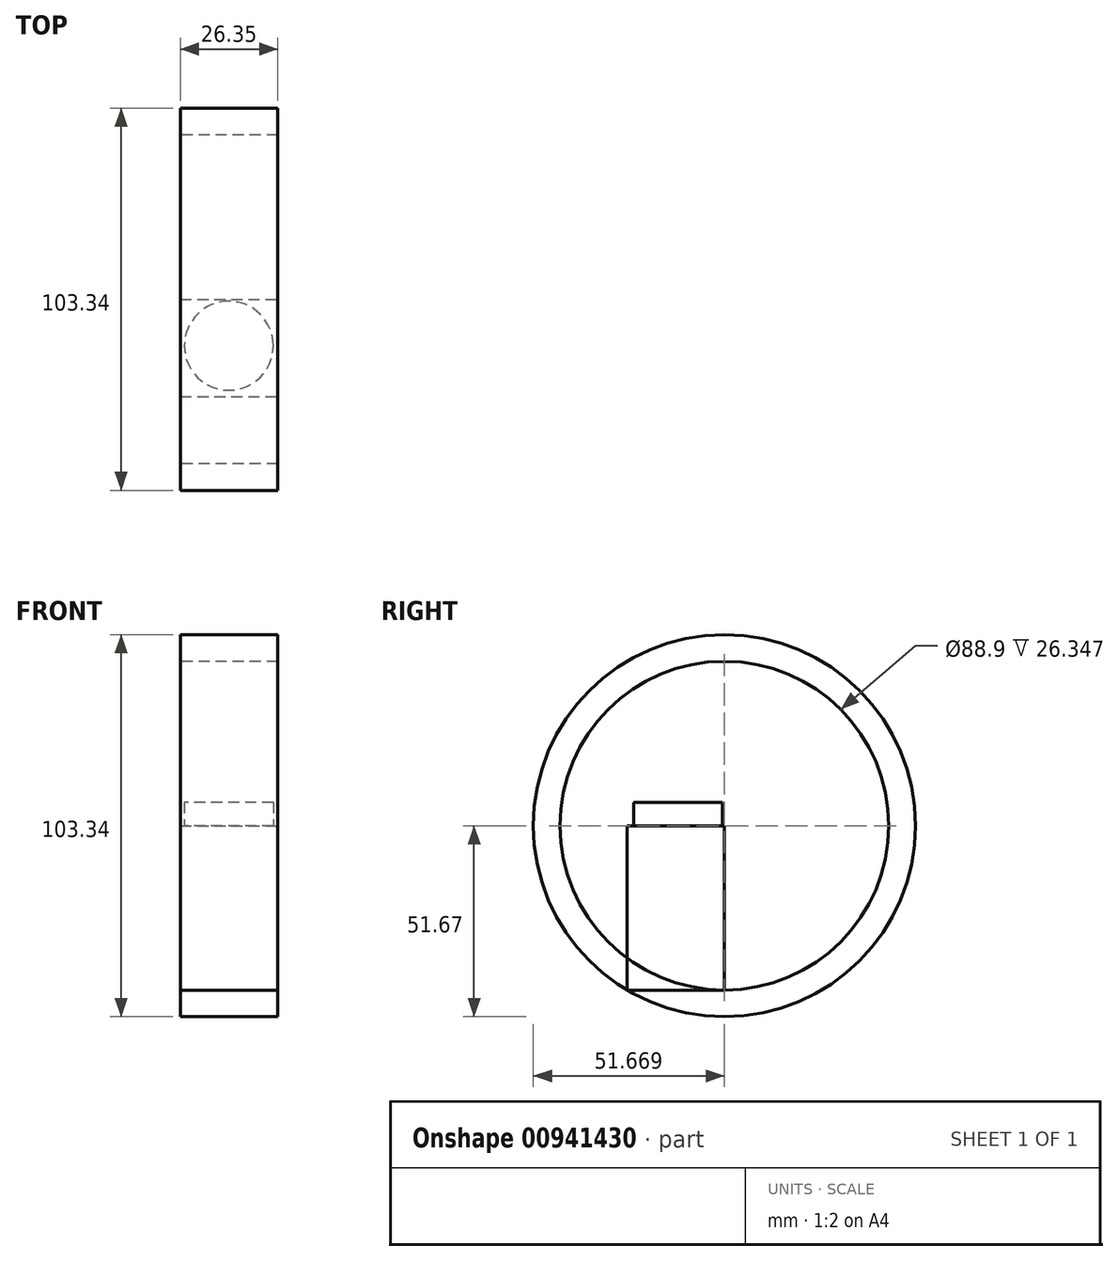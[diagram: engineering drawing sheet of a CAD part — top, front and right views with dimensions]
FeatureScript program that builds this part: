
annotation { "Feature Type Name" : "Feature", "Feature Type Description" : "" }
export const myFeature = defineFeature(function(context is Context, id is Id, definition is map)
    precondition{}
    {
        {
            var Q0;
            Q0=qCreatedBy(makeId("Top.planeOp"),FACE);
            var sketch = newSketch(context, id + "F0", { "sketchPlane" : qUnion([Q0])});
            skLineSegment(sketch, "E0.bottom", {"start": v(-28.65, 33.83) * mm, "end": v(-2.3, 33.83) * mm});
            skLineSegment(sketch, "E0.top", {"start": v(-28.65, 7.48) * mm, "end": v(-2.3, 7.48) * mm});
            skLineSegment(sketch, "E0.left", {"start": v(-28.65, 33.83) * mm, "end": v(-28.65, 7.48) * mm});
            skLineSegment(sketch, "E0.right", {"start": v(-2.3, 33.83) * mm, "end": v(-2.3, 7.48) * mm});
            skSolve(sketch);
        }
        {
            var Q0;
            Q0=qCreatedBy(makeId("Top.planeOp"),FACE);
            var sketch = newSketch(context, id + "F1", { "sketchPlane" : qUnion([Q0])});
            skCircle(sketch, "E1", {"center": v(-15.53, 21.26) * mm, "radius": 12.02 * mm});
            skSolve(sketch);
        }
        {
            var Q0;
            Q0=makeQuery(id+"F1.imprint","IMPRINT",FACE,{"disambiguationData":[TD([[makeQuery(id+"F1.imprint","IMPRINT",EDGE,{"derivedFrom":sQuery(id+"F1.wireOp",EDGE,"E1")}),1.0]])]});
            extrude(context, id + "F2", {"entities" : qUnion([Q0]), "depth" : 50.8 * mm, "offsetDistance" : 25.4 * mm});
        }
        {
            var Q0;
            Q0=makeQuery(id+"F0.imprint","IMPRINT",FACE,{"disambiguationData":[TD([[makeQuery(id+"F0.imprint","IMPRINT",EDGE,{"derivedFrom":sQuery(id+"F0.wireOp",EDGE,"E0.bottom")}),-1.0]])]});
            extrude(context, id + "F3", {"entities" : qUnion([Q0]), "operationType" : NewBodyOperationType.ADD, "depth" : 44.45 * mm, "offsetDistance" : 25.4 * mm});
        }
        {
            var Q0;
            Q0=makeQuery(id+"F2.opExtrude","CAP_EDGE",EDGE,{"disambiguationData":[OSD([sQuery(id+"F1.wireOp",EDGE,"E1")])],"isStart":false});
            var Q1;
            Q1=makeQuery(id+"F3.opExtrude","CAP_EDGE",EDGE,{"disambiguationData":[OSD([sQuery(id+"F0.wireOp",EDGE,"E0.top")])],"isStart":false});
            revolve(context, id + "F4", {"bodyType" : ToolBodyType.SURFACE, "surfaceOperationType" : NewSurfaceOperationType.NEW, "surfaceEntities" : qUnion([Q0]), "axis" : qUnion([Q1]), "revolveType" : RevolveType.FULL});
        }
        {
            var Q0;
            Q0=makeQuery(id+"F0.imprint","IMPRINT",FACE,{"disambiguationData":[TD([[makeQuery(id+"F0.imprint","IMPRINT",EDGE,{"derivedFrom":sQuery(id+"F0.wireOp",EDGE,"E0.bottom")}),-1.0]])]});
            var Q1;
            Q1=makeQuery(id+"F3.opExtrude","CAP_EDGE",EDGE,{"disambiguationData":[OSD([sQuery(id+"F0.wireOp",EDGE,"E0.bottom")])],"isStart":false});
            revolve(context, id + "F5", {"surfaceOperationType" : NewSurfaceOperationType.NEW, "entities" : qUnion([Q0]), "axis" : qUnion([Q1]), "revolveType" : RevolveType.FULL});
        }
    });
